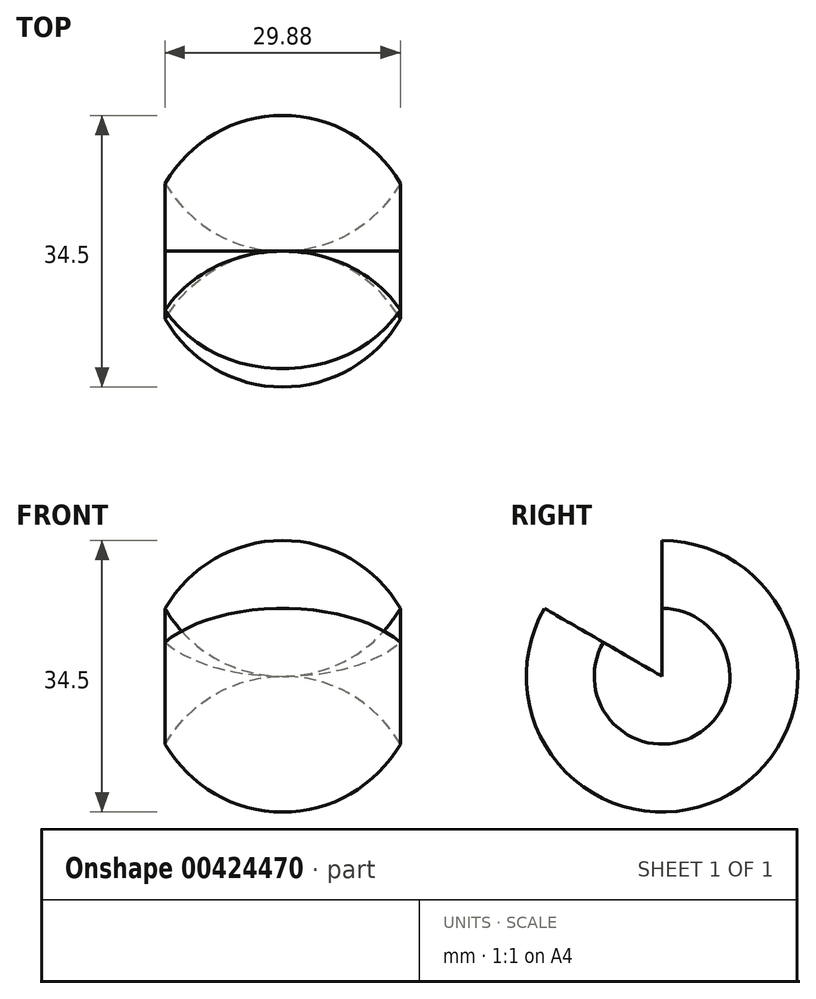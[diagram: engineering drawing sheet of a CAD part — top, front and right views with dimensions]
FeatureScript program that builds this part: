
annotation { "Feature Type Name" : "Feature", "Feature Type Description" : "" }
export const myFeature = defineFeature(function(context is Context, id is Id, definition is map)
    precondition{}
    {
        {
            var Q0;
            Q0=qCreatedBy(makeId("Front.planeOp"),FACE);
            var sketch = newSketch(context, id + "F0", { "sketchPlane" : qUnion([Q0])});
            skArc(sketch, "E0", {"start": v(-14.94, 8.62) * mm, "mid": v(0, 0) * mm, "end": v(14.94, 8.62) * mm});
            skArc(sketch, "E1", {"start": v(14.94, 8.62) * mm, "mid": v(0, 17.25) * mm, "end": v(-14.94, 8.62) * mm});
            skLineSegment(sketch, "E2", {"start": v(0, 0) * mm, "end": v(-48.11, 0) * mm});
            skSolve(sketch);
        }
        {
            var Q0;
            Q0 = qSketchRegion(id + "F0", true);
            var Q1;
            Q1=sQuery(id+"F0.wireOp",EDGE,"E2");
            revolve(context, id + "F1", {"entities" : qUnion([Q0]), "axis" : qUnion([Q1]), "revolveType" : RevolveType.ONE_DIRECTION, "angle" : 300 * degree});
        }
    });
